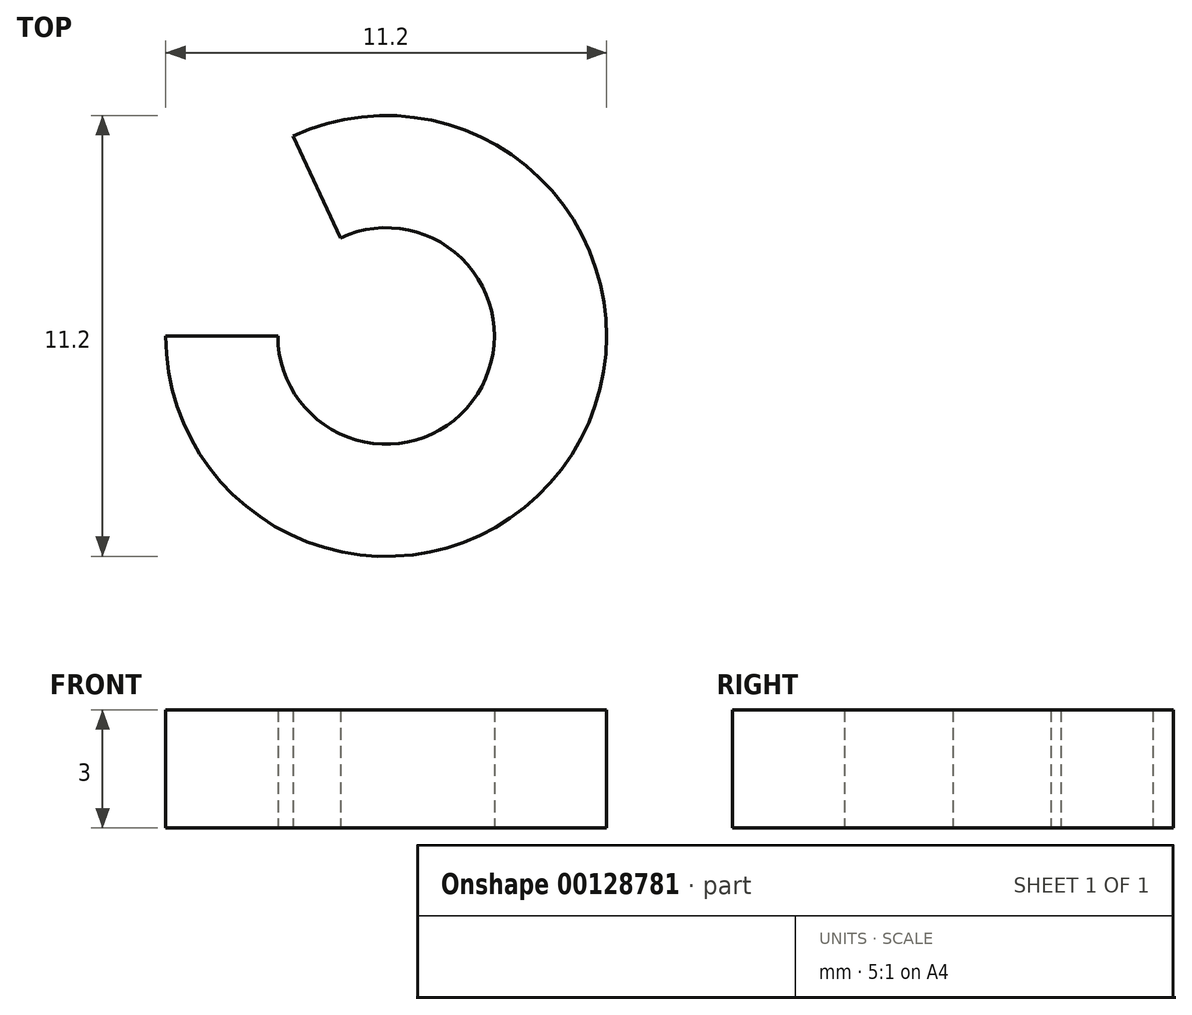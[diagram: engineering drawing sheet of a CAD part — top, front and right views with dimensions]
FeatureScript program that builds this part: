
annotation { "Feature Type Name" : "Feature", "Feature Type Description" : "" }
export const myFeature = defineFeature(function(context is Context, id is Id, definition is map)
    precondition{}
    {
        {
            var Q0;
            Q0=qCreatedBy(makeId("Top.planeOp"),FACE);
            var sketch = newSketch(context, id + "F0", { "sketchPlane" : qUnion([Q0])});
            skArc(sketch, "E0", {"start": v(-2.75, 0) * mm, "mid": v(2.32, -1.48) * mm, "end": v(-1.16, 2.5) * mm});
            skArc(sketch, "E1", {"start": v(-5.6, 0) * mm, "mid": v(4.72, -3) * mm, "end": v(-2.37, 5.08) * mm});
            skLineSegment(sketch, "E2", {"start": v(-2.75, 0) * mm, "end": v(-5.6, 0) * mm});
            skLineSegment(sketch, "E3", {"start": v(-1.16, 2.5) * mm, "end": v(-2.37, 5.08) * mm});
            skSolve(sketch);
        }
        {
            var Q0;
            Q0 = qSketchRegion(id + "F0", true);
            extrude(context, id + "F1", {"entities" : qUnion([Q0]), "depth" : 3 * mm});
        }
    });
